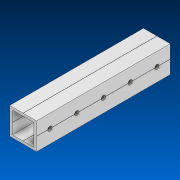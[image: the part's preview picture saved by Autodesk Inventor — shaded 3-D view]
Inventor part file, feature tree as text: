
AUTODESK INVENTOR PART (.ipt)
format: ipt  version: 2022.2 (Build 262287000, 287)  size: 644,096 bytes
history: native  units: in
note: dims shown in document units (in); Inventor stores cm internally (conversion verified against a paired STEP export)
features: other x5, extrude x1, pattern_linear x1, sketch x1, pattern_circular x1
ambient origin geometry x8: Origin, YZ Plane, XZ Plane, XY Plane, X Axis, Y Axis, Z Axis, Center Point
bodies: Solid1 (feature_tree)
feature tree (9):
  extrude  "Extrusion1"  Depth=1.0in
  other  "Work Axis1"
  pattern_linear  "Rectangular Pattern1"  Spacing1=0.0in  [1 undecoded]
  sketch  "Sketch1"  dims[d0=1.0in d1=54.0in d2=0.0in d3=1.9685in d5=1.0in]
  other  "Work Axis2"
  other  "Work Axis3"
  other  "Work Axis4"
  other  "Work Axis5"
  pattern_circular  "CirPattern2"
note: 1 required parameter value undecoded (feature->parameter linkage not recoverable at this tier; creation-order binding heuristic only, values carry confidence <= 0.55)
